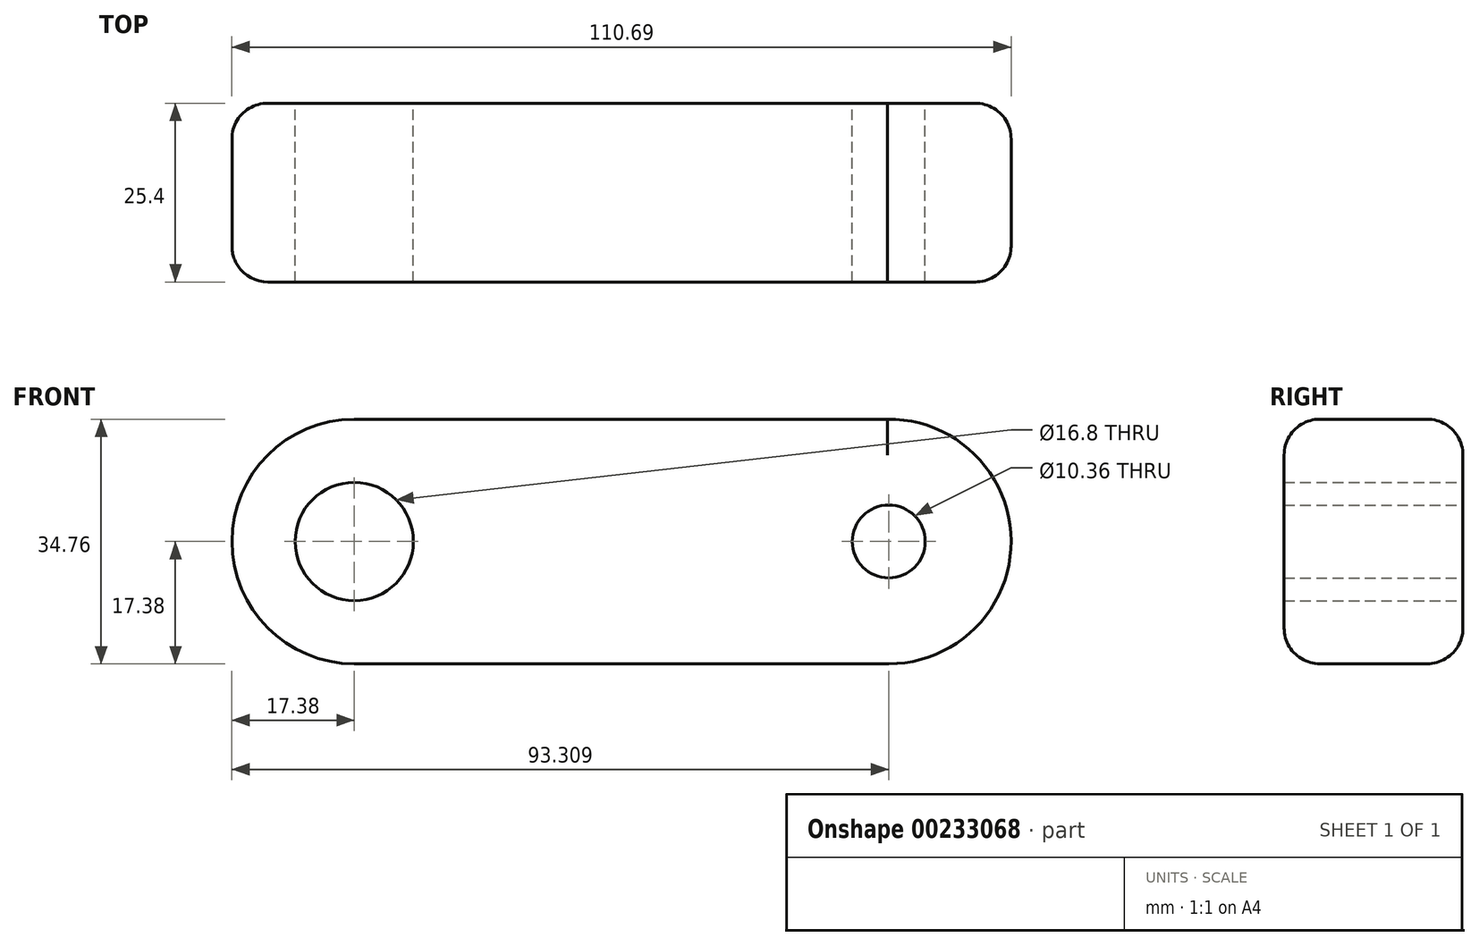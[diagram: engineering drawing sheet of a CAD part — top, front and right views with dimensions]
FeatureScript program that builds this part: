
annotation { "Feature Type Name" : "Feature", "Feature Type Description" : "" }
export const myFeature = defineFeature(function(context is Context, id is Id, definition is map)
    precondition{}
    {
        {
            var Q0;
            Q0=qCreatedBy(makeId("Front.planeOp"),FACE);
            var sketch = newSketch(context, id + "F0", { "sketchPlane" : qUnion([Q0])});
            skCircle(sketch, "E0", {"center": v(0, 0) * mm, "radius": 17.38 * mm});
            skCircle(sketch, "E1", {"center": v(75.93, 0) * mm, "radius": 17.38 * mm});
            skLineSegment(sketch, "E2", {"start": v(0, 17.38) * mm, "end": v(76.12, 17.38) * mm});
            skLineSegment(sketch, "E3", {"start": v(0, -17.38) * mm, "end": v(76.12, -17.38) * mm});
            skCircle(sketch, "E4", {"center": v(0, 0) * mm, "radius": 8.4 * mm});
            skCircle(sketch, "E5", {"center": v(75.93, 0) * mm, "radius": 5.18 * mm});
            skSolve(sketch);
        }
        {
            var Q0;
            Q0 = qSketchRegion(id + "F0", true);
            extrude(context, id + "F1", {"entities" : qUnion([Q0]), "offsetDistance" : 25.4 * mm, "depth" : 25.4 * mm});
        }
        {
            var Q0;
            Q0=makeQuery(id+"F1.opExtrude","CAP_EDGE",EDGE,{"disambiguationData":[OSD([sQuery(id+"F0.wireOp",EDGE,"E0")])],"isStart":false});
            var Q1;
            Q1=makeQuery(id+"F1.opExtrude","CAP_EDGE",EDGE,{"disambiguationData":[OSD([sQuery(id+"F0.wireOp",EDGE,"E2")])],"isStart":false});
            var Q2;
            Q2=makeQuery(id+"F1.opExtrude","CAP_EDGE",EDGE,{"disambiguationData":[OSD([sQuery(id+"F0.wireOp",EDGE,"E1")])],"isStart":false});
            var Q3;
            Q3=makeQuery(id+"F1.opExtrude","CAP_EDGE",EDGE,{"disambiguationData":[OSD([sQuery(id+"F0.wireOp",EDGE,"E3")])],"isStart":false});
            fillet(context, id + "F2", {"entities" : qUnion([Q0, Q1, Q2, Q3]), "radius" : 5.08 * mm, "tangentPropagation" : true, "allowEdgeOverflow" : false});
        }
        {
            var Q0;
            Q0=makeQuery(id+"F1.opExtrude","CAP_EDGE",EDGE,{"disambiguationData":[OSD([sQuery(id+"F0.wireOp",EDGE,"E0")])],"isStart":true});
            var Q1;
            Q1=makeQuery(id+"F1.opExtrude","CAP_EDGE",EDGE,{"disambiguationData":[OSD([sQuery(id+"F0.wireOp",EDGE,"E3")])],"isStart":true});
            var Q2;
            Q2=makeQuery(id+"F1.opExtrude","CAP_EDGE",EDGE,{"disambiguationData":[OSD([sQuery(id+"F0.wireOp",EDGE,"E1")])],"isStart":true});
            var Q3;
            Q3=makeQuery(id+"F1.opExtrude","CAP_EDGE",EDGE,{"disambiguationData":[OSD([sQuery(id+"F0.wireOp",EDGE,"E2")])],"isStart":true});
            fillet(context, id + "F3", {"entities" : qUnion([Q0, Q1, Q2, Q3]), "radius" : 5.08 * mm, "tangentPropagation" : true, "allowEdgeOverflow" : false});
        }
    });
